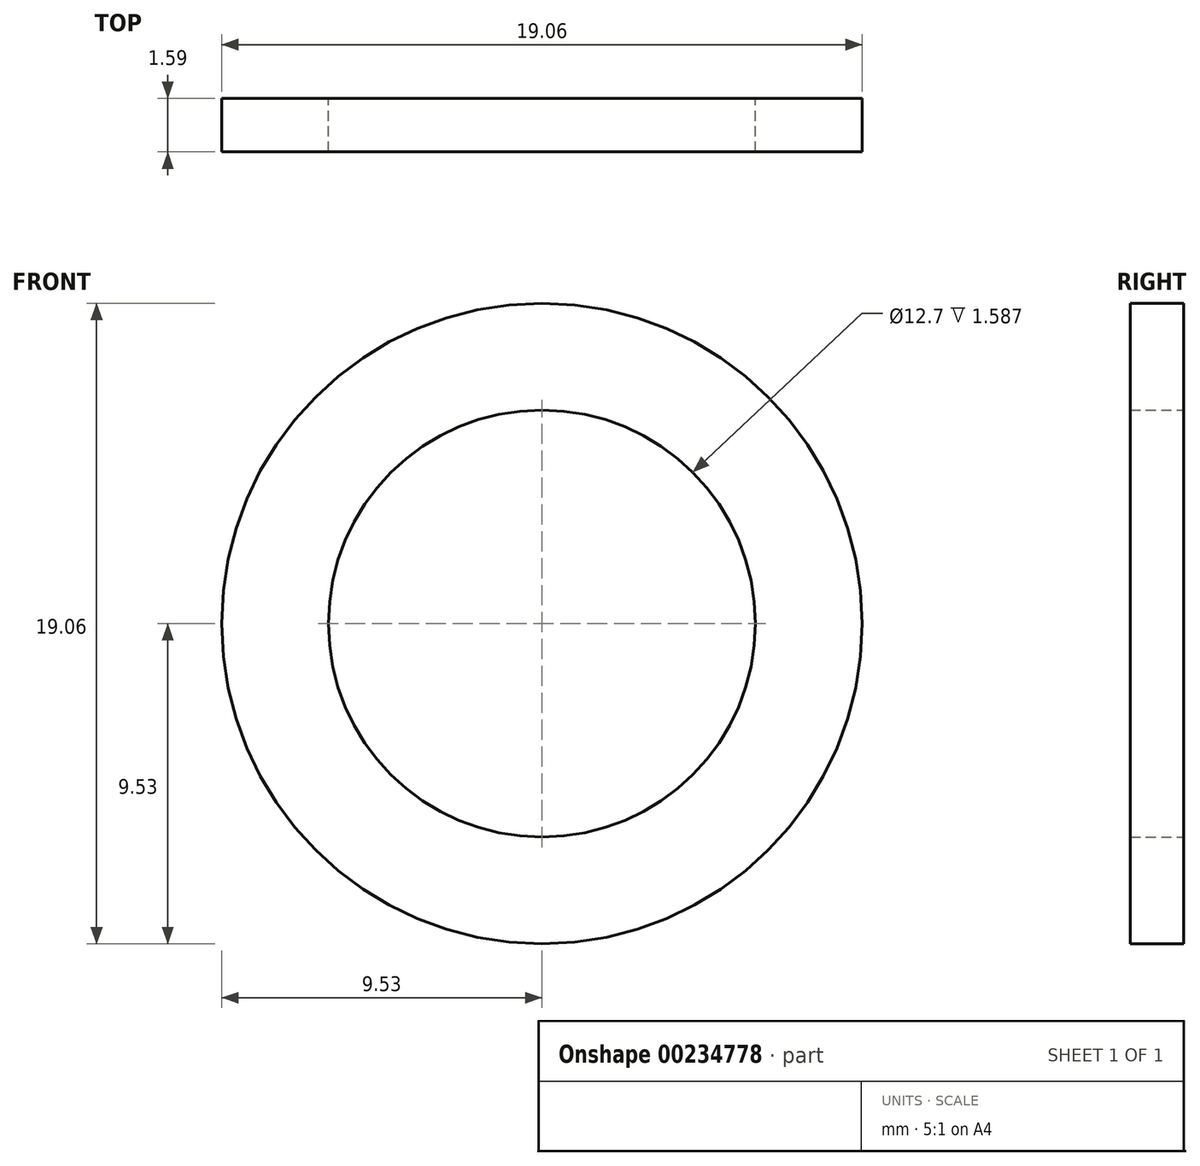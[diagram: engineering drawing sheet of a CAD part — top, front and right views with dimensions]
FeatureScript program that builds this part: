
annotation { "Feature Type Name" : "Feature", "Feature Type Description" : "" }
export const myFeature = defineFeature(function(context is Context, id is Id, definition is map)
    precondition{}
    {
        {
            var Q0;
            Q0=qCreatedBy(makeId("Front.planeOp"),FACE);
            var sketch = newSketch(context, id + "F1", { "sketchPlane" : qUnion([Q0])});
            skCircle(sketch, "E0", {"center": v(0, 0) * mm, "radius": 6.35 * mm});
            skCircle(sketch, "E1", {"center": v(0, 0) * mm, "radius": 9.53 * mm});
            skSolve(sketch);
        }
        {
            var Q0;
            Q0=makeQuery(id+"F1.imprint","IMPRINT",FACE,{"disambiguationData":[TD([[makeQuery(id+"F1.imprint","IMPRINT",EDGE,{"derivedFrom":sQuery(id+"F1.wireOp",EDGE,"E0")}),-1.0]])]});
            extrude(context, id + "F0", {"entities" : qUnion([Q0]), "depth" : 1.59 * mm});
        }
    });
